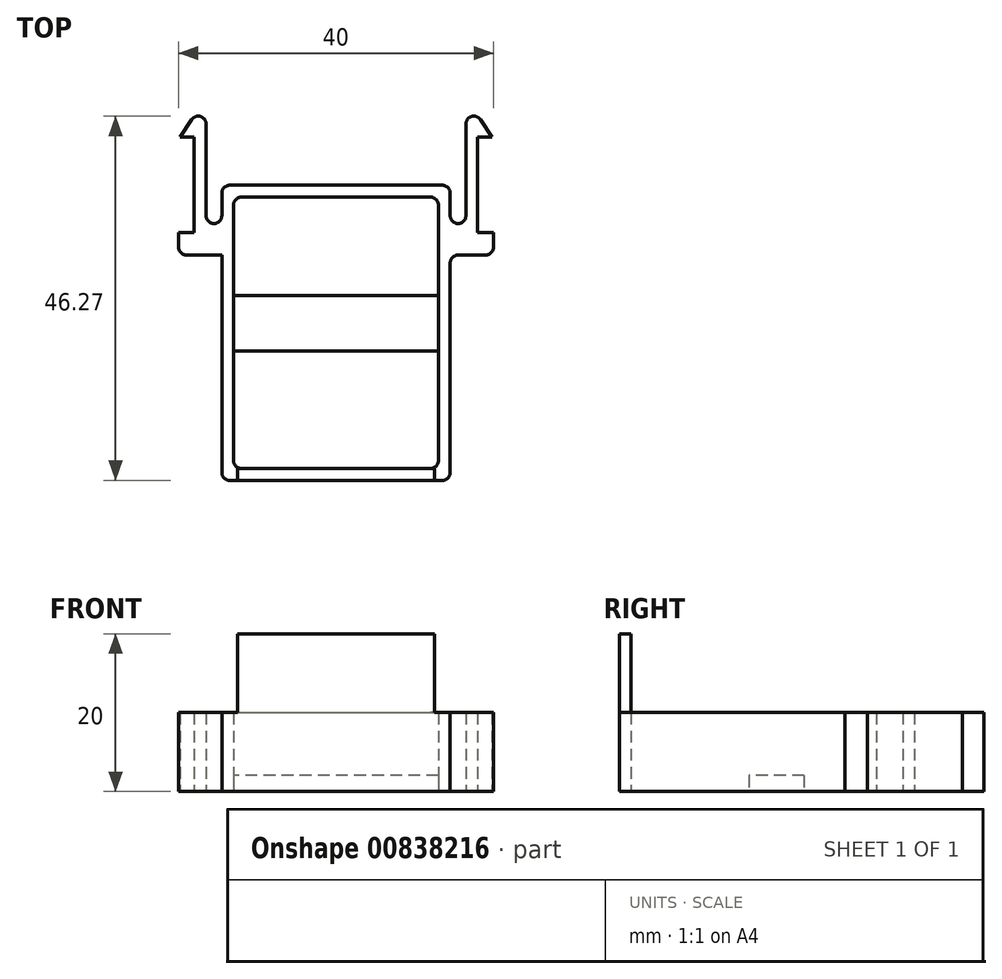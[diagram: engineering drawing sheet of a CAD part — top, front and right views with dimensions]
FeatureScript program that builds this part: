
annotation { "Feature Type Name" : "Feature", "Feature Type Description" : "" }
export const myFeature = defineFeature(function(context is Context, id is Id, definition is map)
    precondition{}
    {
        {
            var Q0;
            Q0=qCreatedBy(makeId("Top.planeOp"),FACE);
            var sketch = newSketch(context, id + "F0", { "sketchPlane" : qUnion([Q0])});
            skLineSegment(sketch, "E0.bottom", {"start": v(-13, 17.25) * mm, "end": v(13, 17.25) * mm});
            skLineSegment(sketch, "E0.top", {"start": v(-13, -17.25) * mm, "end": v(13, -17.25) * mm});
            skLineSegment(sketch, "E0.left", {"start": v(-13, 17.25) * mm, "end": v(-13, -17.25) * mm});
            skLineSegment(sketch, "E0.right", {"start": v(13, 17.25) * mm, "end": v(13, -17.25) * mm});
            skPoint(sketch, "E0.middle", {"position": v(0, 0) * mm});
            skLineSegment(sketch, "E1.0", {"start": v(-14.5, 18.75) * mm, "end": v(-14.5, -18.75) * mm});
            skLineSegment(sketch, "E1.1", {"start": v(-14.5, 18.75) * mm, "end": v(14.5, 18.75) * mm});
            skLineSegment(sketch, "E1.2", {"start": v(14.5, 18.75) * mm, "end": v(14.5, -18.75) * mm});
            skLineSegment(sketch, "E1.3", {"start": v(-14.5, -18.75) * mm, "end": v(14.5, -18.75) * mm});
            skLineSegment(sketch, "E2", {"start": v(0, -36.25) * mm, "end": v(0, 59.39) * mm, "construction": true});
            skLineSegment(sketch, "E3", {"start": v(-14.5, 9.88) * mm, "end": v(-16.5, 9.88) * mm});
            skLineSegment(sketch, "E4", {"start": v(-16.5, 9.88) * mm, "end": v(-16.5, 13.88) * mm});
            skLineSegment(sketch, "E5", {"start": v(-16.5, 13.88) * mm, "end": v(-14.5, 13.88) * mm});
            skLineSegment(sketch, "E6", {"start": v(-16.5, 9.88) * mm, "end": v(-16.5, 29.86) * mm});
            skLineSegment(sketch, "E7", {"start": v(-16.5, 29.86) * mm, "end": v(-19.8, 24.85) * mm});
            skLineSegment(sketch, "E8", {"start": v(-19.8, 24.85) * mm, "end": v(-18, 24.85) * mm});
            skLineSegment(sketch, "E9", {"start": v(-18, 24.85) * mm, "end": v(-18, 9.88) * mm});
            skLineSegment(sketch, "E10", {"start": v(-18, 9.88) * mm, "end": v(-16.5, 9.88) * mm});
            skLineSegment(sketch, "E11", {"start": v(-18, 9.88) * mm, "end": v(-20, 9.88) * mm});
            skLineSegment(sketch, "E12", {"start": v(-20, 9.88) * mm, "end": v(-20, 12.75) * mm});
            skLineSegment(sketch, "E13", {"start": v(-20, 12.75) * mm, "end": v(-18, 12.75) * mm});
            skLineSegment(sketch, "E14.MirrorCS", {"start": v(16.5, 9.88) * mm, "end": v(16.5, 29.86) * mm});
            skLineSegment(sketch, "E15.MirrorCS", {"start": v(16.5, 29.86) * mm, "end": v(19.8, 24.85) * mm});
            skLineSegment(sketch, "E16.MirrorCS", {"start": v(18, 24.85) * mm, "end": v(18, 9.88) * mm});
            skLineSegment(sketch, "E17.MirrorCS", {"start": v(20, 12.75) * mm, "end": v(18, 12.75) * mm});
            skLineSegment(sketch, "E18.MirrorCS", {"start": v(20, 9.88) * mm, "end": v(20, 12.75) * mm});
            skLineSegment(sketch, "E19.MirrorCS", {"start": v(18, 9.88) * mm, "end": v(20, 9.88) * mm});
            skLineSegment(sketch, "E20.MirrorCS", {"start": v(18, 9.88) * mm, "end": v(16.5, 9.88) * mm});
            skLineSegment(sketch, "E21.MirrorCS", {"start": v(14.5, 9.88) * mm, "end": v(16.5, 9.88) * mm});
            skLineSegment(sketch, "E22.MirrorCS", {"start": v(16.5, 13.88) * mm, "end": v(14.5, 13.88) * mm});
            skLineSegment(sketch, "E23.MirrorCS", {"start": v(19.8, 24.85) * mm, "end": v(18, 24.85) * mm});
            skLineSegment(sketch, "E24", {"start": v(-13, -2.29) * mm, "end": v(13, -2.29) * mm});
            skLineSegment(sketch, "E25", {"start": v(13, -2.29) * mm, "end": v(13, 4.71) * mm});
            skLineSegment(sketch, "E26", {"start": v(13, 4.71) * mm, "end": v(-13, 4.71) * mm});
            skSolve(sketch);
        }
        {
            var Q0;
            Q0=qSketchRegion(id+"F0",true);
            extrude(context, id + "F1", {"entities" : qUnion([Q0]), "depth" : 10 * mm, "offsetDistance" : 25 * mm});
        }
        {
            var Q0;
            Q0=makeQuery(id+"F1.opExtrude","SWEPT_EDGE",EDGE,{"disambiguationData":[OSD([sQuery(id+"F0.wireOp",EDGE,"E1.0"),sQuery(id+"F0.wireOp",EDGE,"E1.1")])]});
            var Q1;
            Q1=makeQuery(id+"F1.opExtrude","SWEPT_EDGE",EDGE,{"disambiguationData":[OSD([sQuery(id+"F0.wireOp",EDGE,"E11"),sQuery(id+"F0.wireOp",EDGE,"E12")])]});
            var Q2;
            Q2=makeQuery(id+"F1.opExtrude","SWEPT_EDGE",EDGE,{"disambiguationData":[OSD([sQuery(id+"F0.wireOp",EDGE,"E1.1"),sQuery(id+"F0.wireOp",EDGE,"E1.2")])]});
            var Q3;
            Q3=makeQuery(id+"F1.opExtrude","SWEPT_EDGE",EDGE,{"disambiguationData":[OSD([sQuery(id+"F0.wireOp",EDGE,"E18.MirrorCS"),sQuery(id+"F0.wireOp",EDGE,"E19.MirrorCS")])]});
            var Q4;
            Q4=makeQuery(id+"F1.opExtrude","SWEPT_EDGE",EDGE,{"disambiguationData":[OSD([sQuery(id+"F0.wireOp",EDGE,"E0.bottom"),sQuery(id+"F0.wireOp",EDGE,"E0.left")])]});
            var Q5;
            Q5=makeQuery(id+"F1.opExtrude","SWEPT_EDGE",EDGE,{"disambiguationData":[OSD([sQuery(id+"F0.wireOp",EDGE,"E1.2"),sQuery(id+"F0.wireOp",EDGE,"E21.MirrorCS")])]});
            var Q6;
            Q6=makeQuery(id+"F1.opExtrude","SWEPT_EDGE",EDGE,{"disambiguationData":[OSD([sQuery(id+"F0.wireOp",EDGE,"E1.2"),sQuery(id+"F0.wireOp",EDGE,"E1.3")])]});
            var Q7;
            Q7=makeQuery(id+"F1.opExtrude","SWEPT_EDGE",EDGE,{"disambiguationData":[OSD([sQuery(id+"F0.wireOp",EDGE,"E1.0"),sQuery(id+"F0.wireOp",EDGE,"E1.3")])]});
            var Q8;
            Q8=makeQuery(id+"F1.opExtrude","SWEPT_EDGE",EDGE,{"disambiguationData":[OSD([sQuery(id+"F0.wireOp",EDGE,"E0.top"),sQuery(id+"F0.wireOp",EDGE,"E0.left")])]});
            var Q9;
            Q9=makeQuery(id+"F1.opExtrude","SWEPT_EDGE",EDGE,{"disambiguationData":[OSD([sQuery(id+"F0.wireOp",EDGE,"E0.bottom"),sQuery(id+"F0.wireOp",EDGE,"E0.right")])]});
            var Q10;
            Q10=makeQuery(id+"F1.opExtrude","SWEPT_EDGE",EDGE,{"disambiguationData":[OSD([sQuery(id+"F0.wireOp",EDGE,"E0.top"),sQuery(id+"F0.wireOp",EDGE,"E0.right")])]});
            var Q11;
            Q11=makeQuery(id+"F1.opExtrude","SWEPT_EDGE",EDGE,{"disambiguationData":[OSD([sQuery(id+"F0.wireOp",EDGE,"E1.0"),sQuery(id+"F0.wireOp",EDGE,"E5")])]});
            var Q12;
            Q12=makeQuery(id+"F1.opExtrude","SWEPT_EDGE",EDGE,{"disambiguationData":[OSD([sQuery(id+"F0.wireOp",EDGE,"E14.MirrorCS"),sQuery(id+"F0.wireOp",EDGE,"E22.MirrorCS")])]});
            var Q13;
            Q13=makeQuery(id+"F1.opExtrude","SWEPT_EDGE",EDGE,{"disambiguationData":[OSD([sQuery(id+"F0.wireOp",EDGE,"E5"),sQuery(id+"F0.wireOp",EDGE,"E6")])]});
            var Q14;
            Q14=makeQuery(id+"F1.opExtrude","SWEPT_EDGE",EDGE,{"disambiguationData":[OSD([sQuery(id+"F0.wireOp",EDGE,"E1.2"),sQuery(id+"F0.wireOp",EDGE,"E22.MirrorCS")])]});
            var Q15;
            Q15=makeQuery(id+"F1.opExtrude","SWEPT_EDGE",EDGE,{"disambiguationData":[OSD([sQuery(id+"F0.wireOp",EDGE,"E6"),sQuery(id+"F0.wireOp",EDGE,"E7")])]});
            var Q16;
            Q16=makeQuery(id+"F1.opExtrude","SWEPT_EDGE",EDGE,{"disambiguationData":[OSD([sQuery(id+"F0.wireOp",EDGE,"E14.MirrorCS"),sQuery(id+"F0.wireOp",EDGE,"E15.MirrorCS")])]});
            fillet(context, id + "F2", {"entities" : qUnion([Q0, Q1, Q2, Q3, Q4, Q5, Q6, Q7, Q8, Q9, Q10, Q11, Q12, Q13, Q14, Q15, Q16]), "radius" : 1 * mm, "tangentPropagation" : true, "allowEdgeOverflow" : false});
        }
        {
            var Q0;
            {var subQ0=sQuery(id+"F0.wireOp",EDGE,"E24");Q0=makeQuery(id+"F0.imprint","IMPRINT",FACE,{"disambiguationData":[TD([[makeQuery(id+"F0.imprint","IMPRINT",EDGE,{"derivedFrom":subQ0}),1.0]])]});}
            extrude(context, id + "F3", {"entities" : qUnion([Q0]), "operationType" : NewBodyOperationType.ADD, "depth" : 2 * mm, "offsetDistance" : 25 * mm});
        }
        {
            var Q0;
            Q0=makeQuery(id+"F1.opExtrude","SWEPT_FACE",FACE,{"disambiguationData":[OSD([sQuery(id+"F0.wireOp",EDGE,"E1.3")])]});
            var sketch = newSketch(context, id + "F4", { "sketchPlane" : qUnion([Q0])});
            skLineSegment(sketch, "E27", {"start": v(-13.5, 5) * mm, "end": v(13.5, 5) * mm, "construction": true});
            skLineSegment(sketch, "E28", {"start": v(0, 10) * mm, "end": v(0, 0) * mm, "construction": true});
            skLineSegment(sketch, "E29.top", {"start": v(-12.49, 20) * mm, "end": v(12.49, 20) * mm});
            skLineSegment(sketch, "E29.left", {"start": v(-12.49, 5) * mm, "end": v(-12.49, 20) * mm});
            skLineSegment(sketch, "E29.right", {"start": v(12.49, 5) * mm, "end": v(12.49, 20) * mm});
            skPoint(sketch, "E29.middle", {"position": v(0, 5) * mm});
            skPoint(sketch, "E30.orphan", {"position": v(-12.49, -10) * mm});
            skPoint(sketch, "E31.orphan", {"position": v(12.49, -10) * mm});
            skLineSegment(sketch, "E32", {"start": v(-12.49, 10) * mm, "end": v(12.49, 10) * mm});
            skSolve(sketch);
        }
        {
            var Q0;
            Q0 = qSketchRegion(id + "F4", true);
            extrude(context, id + "F5", {"entities" : qUnion([Q0]), "operationType" : NewBodyOperationType.ADD, "oppositeDirection" : true, "depth" : 1.5 * mm, "offsetDistance" : 25 * mm});
        }
    });
